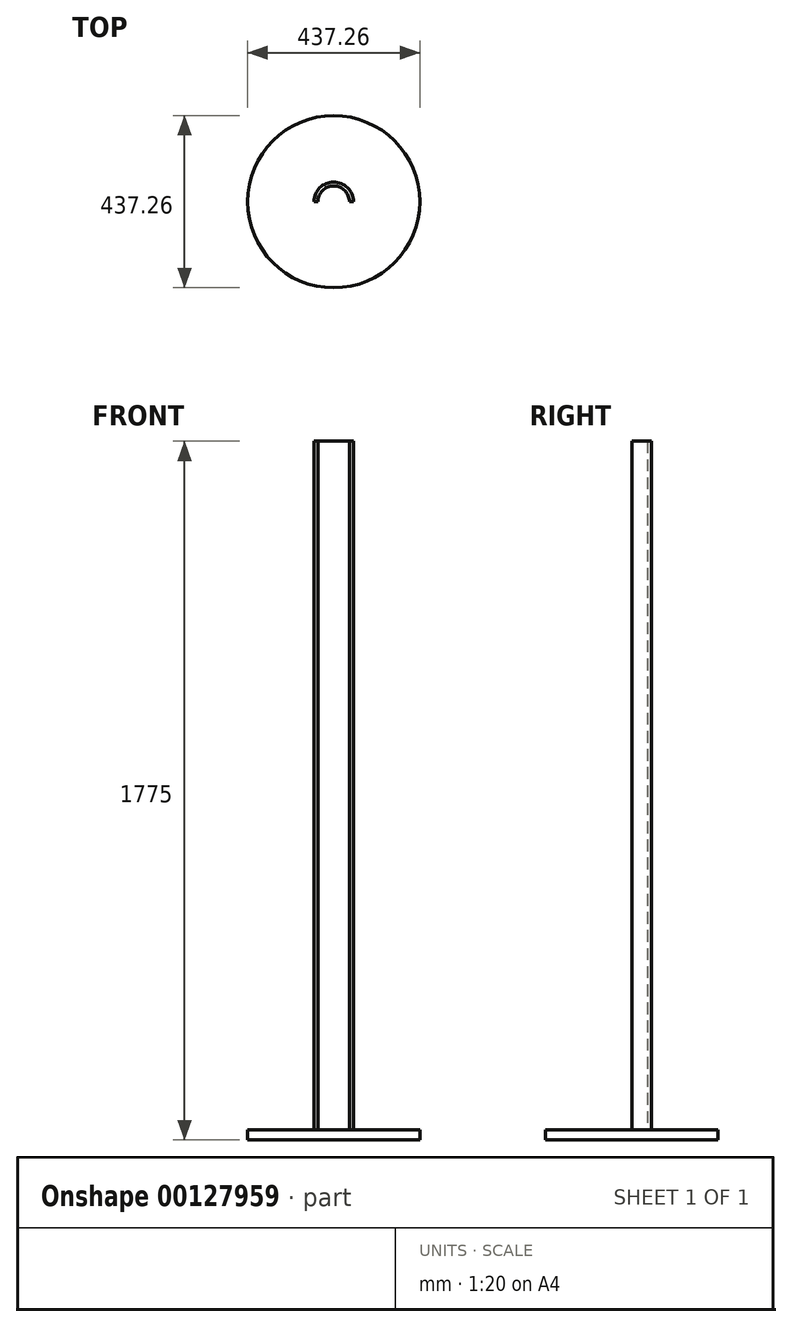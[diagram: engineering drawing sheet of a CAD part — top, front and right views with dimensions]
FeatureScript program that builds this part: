
annotation { "Feature Type Name" : "Feature", "Feature Type Description" : "" }
export const myFeature = defineFeature(function(context is Context, id is Id, definition is map)
    precondition{}
    {
        {
            var Q0;
            Q0=qCreatedBy(makeId("Top.planeOp"),FACE);
            var sketch = newSketch(context, id + "F0", { "sketchPlane" : qUnion([Q0])});
            skArc(sketch, "E0", {"start": v(50, 0) * mm, "mid": v(0, 50) * mm, "end": v(-50, 0) * mm});
            skArc(sketch, "E1", {"start": v(40, 0) * mm, "mid": v(0, 40) * mm, "end": v(-40, 0) * mm});
            skLineSegment(sketch, "E2", {"start": v(-50, 0) * mm, "end": v(50, 0) * mm});
            skSolve(sketch);
        }
        {
            var Q0;
            {var subQ0=sQuery(id+"F0.wireOp",EDGE,"E0");Q0=makeQuery(id+"F0.imprint","IMPRINT",FACE,{"disambiguationData":[TD([[makeQuery(id+"F0.imprint","IMPRINT",EDGE,{"derivedFrom":subQ0}),1.0]])]});}
            extrude(context, id + "F1", {"entities" : qUnion([Q0]), "depth" : 1750 * mm});
        }
        {
            var Q0;
            Q0=makeQuery(id+"F1.opExtrude","CAP_FACE",FACE,{"disambiguationData":[OSD([sQuery(id+"F0.wireOp",EDGE,"E0"),sQuery(id+"F0.wireOp",EDGE,"E1"),sQuery(id+"F0.wireOp",EDGE,"E2")])],"isStart":true});
            var sketch = newSketch(context, id + "F2", { "sketchPlane" : qUnion([Q0])});
            skCircle(sketch, "E3", {"center": v(0, 0) * mm, "radius": 218.63 * mm});
            skSolve(sketch);
        }
        {
            var Q0;
            Q0=makeQuery(id+"F2.imprint","IMPRINT",FACE,{"disambiguationData":[TD([[makeQuery(id+"F2.imprint","IMPRINT",EDGE,{"derivedFrom":sQuery(id+"F2.wireOp",EDGE,"E3")}),1.0]])]});
            var Q1;
            {var subQ0=sQuery(id+"F0.wireOp",EDGE,"E0");Q1=makeQuery(id+"F2.imprint","IMPRINT",FACE,{"disambiguationData":[TD([[makeQuery(id+"F2.imprint","IMPRINT",EDGE,{"derivedFrom":makeQuery(id+"F1.opExtrude","CAP_EDGE",EDGE,{"disambiguationData":[OSD([subQ0])],"isStart":true})}),-1.0]])]});}
            extrude(context, id + "F3", {"entities" : qUnion([Q0, Q1]), "depth" : 25 * mm});
        }
    });
